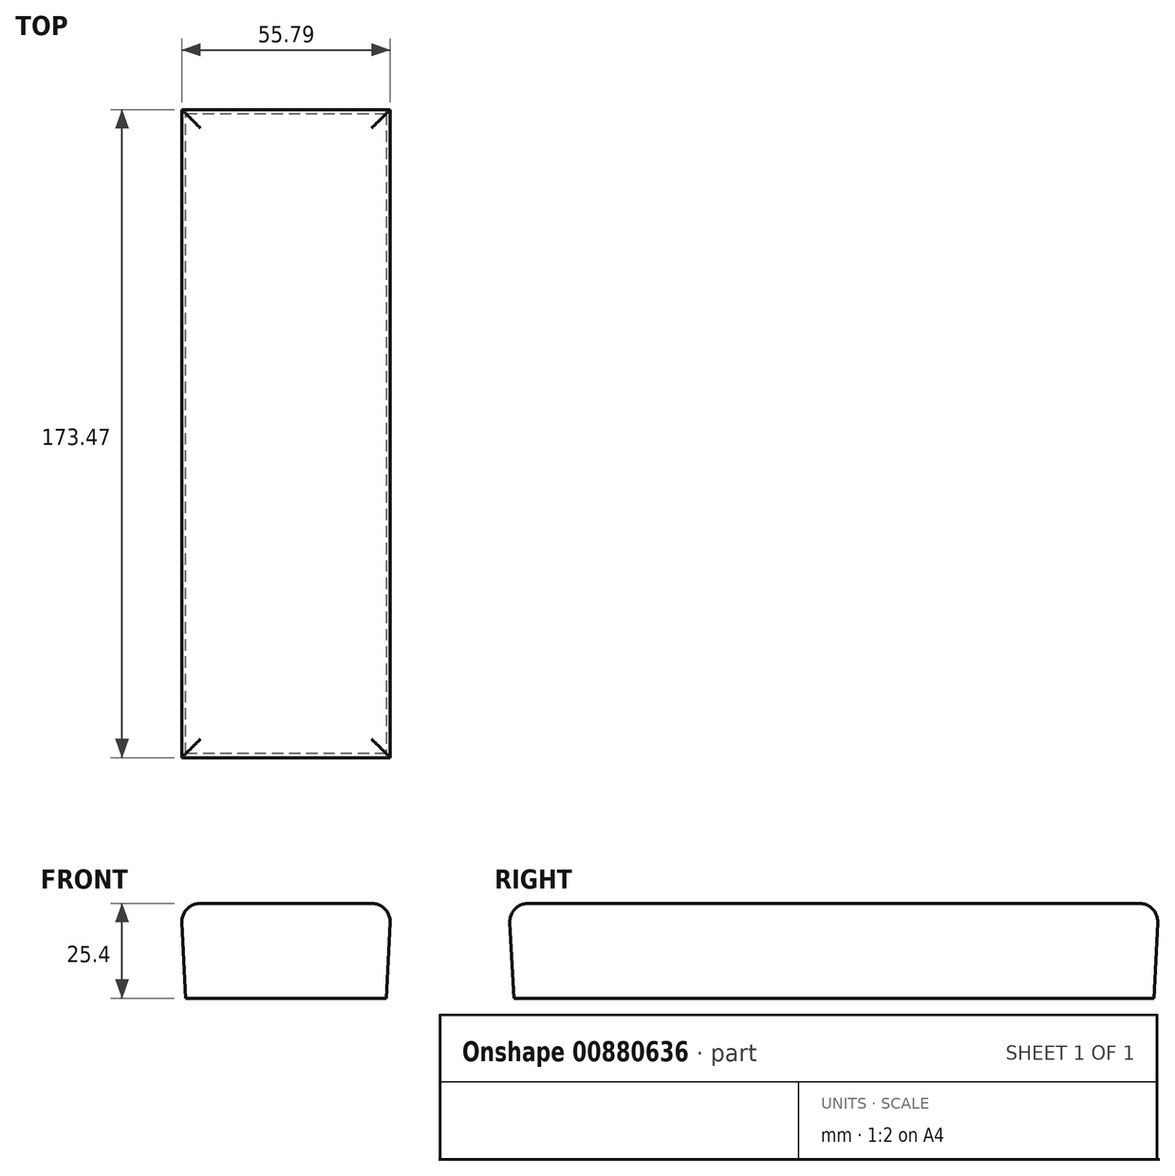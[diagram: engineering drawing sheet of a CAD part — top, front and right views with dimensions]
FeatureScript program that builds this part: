
annotation { "Feature Type Name" : "Feature", "Feature Type Description" : "" }
export const myFeature = defineFeature(function(context is Context, id is Id, definition is map)
    precondition{}
    {
        {
            var Q0;
            Q0=qCreatedBy(makeId("Top.planeOp"),FACE);
            var sketch = newSketch(context, id + "F0", { "sketchPlane" : qUnion([Q0])});
            skLineSegment(sketch, "E0", {"start": v(0, 0) * mm, "end": v(0, 171.35) * mm});
            skLineSegment(sketch, "E1", {"start": v(0, 171.35) * mm, "end": v(53.67, 171.35) * mm});
            skLineSegment(sketch, "E2", {"start": v(53.67, 171.35) * mm, "end": v(53.67, 0) * mm});
            skLineSegment(sketch, "E3", {"start": v(53.67, 0) * mm, "end": v(0, 0) * mm});
            skSolve(sketch);
        }
        {
            var Q0;
            Q0=makeQuery(id+"F0.imprint","IMPRINT",FACE,{"disambiguationData":[TD([[makeQuery(id+"F0.imprint","IMPRINT",EDGE,{"derivedFrom":sQuery(id+"F0.wireOp",EDGE,"E0")}),-1.0]])]});
            var sketch = newSketch(context, id + "F1", { "sketchPlane" : qUnion([Q0])});
            skSolve(sketch);
        }
        {
            var Q0;
            Q0=makeQuery(id+"F1.imprint","IMPRINT",FACE,{"disambiguationData":[TD([[makeQuery(id+"F1.imprint","IMPRINT",EDGE,{"derivedFrom":makeQuery(id+"F0.imprint","IMPRINT",EDGE,{"derivedFrom":sQuery(id+"F0.wireOp",EDGE,"E0")})}),-1.0]])]});
            var sketch = newSketch(context, id + "F2", { "sketchPlane" : qUnion([Q0])});
            skCircle(sketch, "E4", {"center": v(27.26, 53.84) * mm, "radius": 54.26 * mm});
            skPoint(sketch, "E4.first.point", {"position": v(0, 100.75) * mm});
            skPoint(sketch, "E4.second.point", {"position": v(55.18, 100.36) * mm});
            skPoint(sketch, "E4.third.point", {"position": v(34.02, 0) * mm});
            skSolve(sketch);
        }
        {
            var Q0;
            Q0=makeQuery(id+"F0.imprint","IMPRINT",FACE,{"disambiguationData":[TD([[makeQuery(id+"F0.imprint","IMPRINT",EDGE,{"derivedFrom":sQuery(id+"F0.wireOp",EDGE,"E0")}),-1.0]])]});
            extrude(context, id + "F3", {"entities" : qUnion([Q0]), "depth" : 25.4 * mm, "offsetDistance" : 25.4 * mm, "hasDraft" : true, "draftAngle" : 3 * degree});
        }
        {
            var Q0;
            Q0=sQuery(id+"F2.wireOp",EDGE,"E4");
            extrude(context, id + "F4", {"bodyType" : ToolBodyType.SURFACE, "surfaceEntities" : qUnion([Q0]), "depth" : 500 * mm, "offsetDistance" : 25.4 * mm});
        }
        {
            var Q0;
            Q0=makeQuery(id+"F4.opExtrude","SWEPT_FACE",FACE,{"disambiguationData":[OSD([sQuery(id+"F2.wireOp",EDGE,"E4")])]});
            var Q1;
            Q1=makeQuery(id+"F3.opExtrude","CAP_FACE",FACE,{"disambiguationData":[OSD([sQuery(id+"F0.wireOp",EDGE,"E0"),sQuery(id+"F0.wireOp",EDGE,"E1"),sQuery(id+"F0.wireOp",EDGE,"E2"),sQuery(id+"F0.wireOp",EDGE,"E3")])],"isStart":false});
            fillet(context, id + "F5", {"entities" : qUnion([Q0, Q1]), "radius" : 5 * mm, "tangentPropagation" : true, "allowEdgeOverflow" : false});
        }
    });
